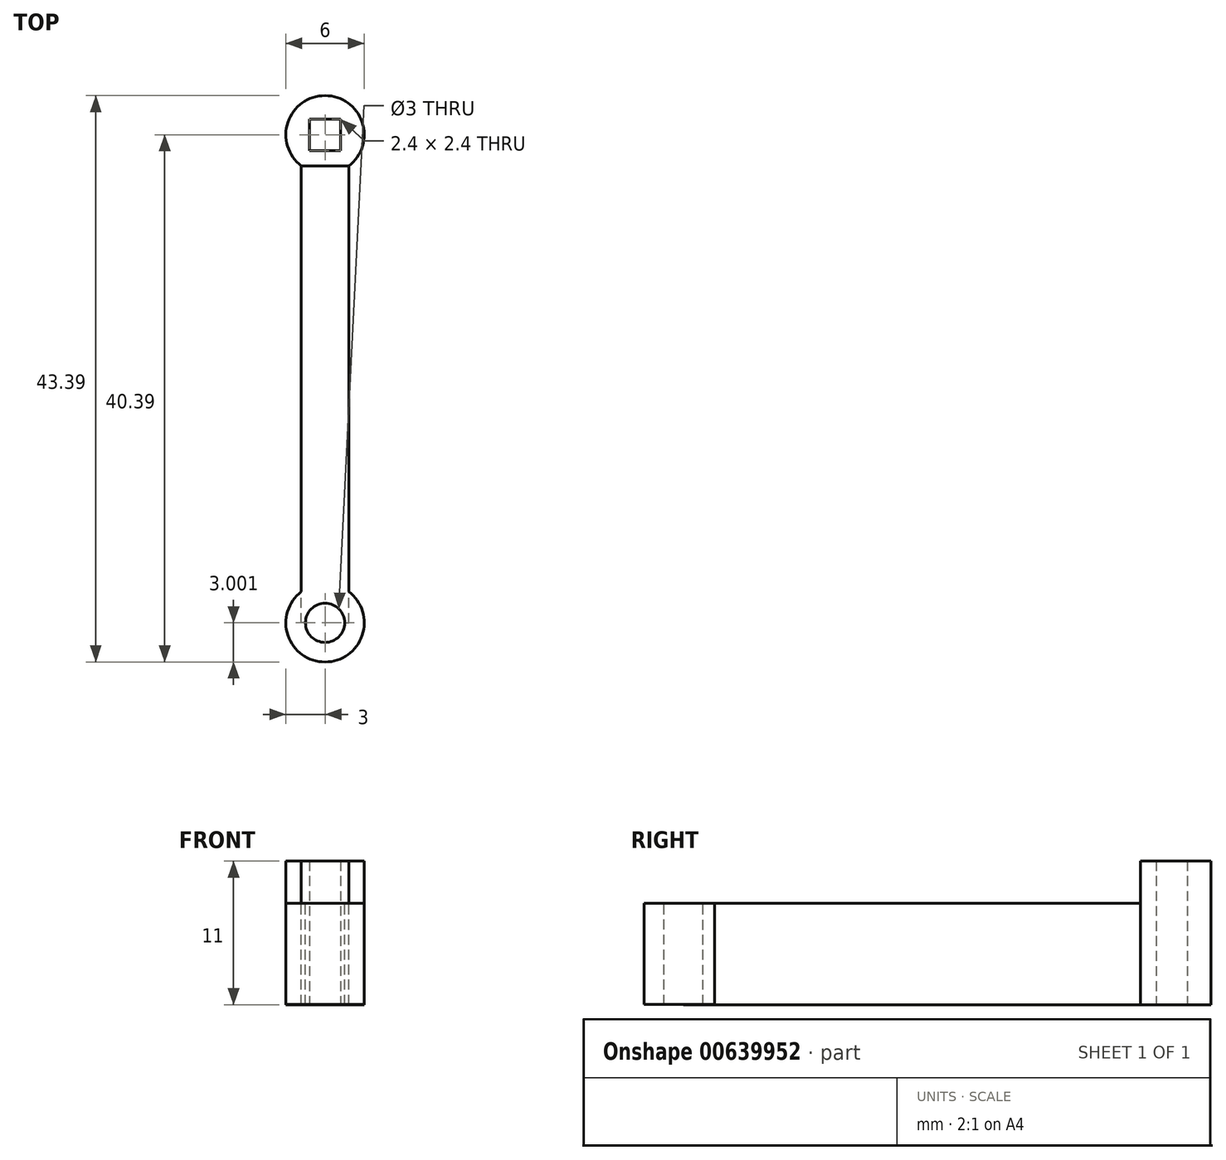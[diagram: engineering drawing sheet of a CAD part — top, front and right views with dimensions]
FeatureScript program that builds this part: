
annotation { "Feature Type Name" : "Feature", "Feature Type Description" : "" }
export const myFeature = defineFeature(function(context is Context, id is Id, definition is map)
    precondition{}
    {
        {
            var Q0;
            Q0=qCreatedBy(makeId("Top.planeOp"),FACE);
            var sketch = newSketch(context, id + "F0", { "sketchPlane" : qUnion([Q0])});
            skCircle(sketch, "E0", {"center": v(0, 0) * mm, "radius": 3 * mm});
            skLineSegment(sketch, "E1", {"start": v(0, 0) * mm, "end": v(0, -3) * mm});
            skLineSegment(sketch, "E2", {"start": v(0, 0) * mm, "end": v(0, 3) * mm});
            skPoint(sketch, "E3", {"position": v(0, -1.2) * mm});
            skPoint(sketch, "E4", {"position": v(0, 1.2) * mm});
            skLineSegment(sketch, "E5", {"start": v(0, 0) * mm, "end": v(3, 0) * mm});
            skLineSegment(sketch, "E6", {"start": v(0, 0) * mm, "end": v(-3, 0) * mm});
            skPoint(sketch, "E7", {"position": v(-1.2, 0) * mm});
            skPoint(sketch, "E8", {"position": v(1.2, 0) * mm});
            skPoint(sketch, "E9", {"position": v(-2.7, 2.32) * mm});
            skLineSegment(sketch, "E10", {"start": v(-1.2, 1.03) * mm, "end": v(-1.2, 0) * mm});
            skLineSegment(sketch, "E11", {"start": v(0, 1.2) * mm, "end": v(1.2, 1.2) * mm});
            skLineSegment(sketch, "E12", {"start": v(1.2, 1.2) * mm, "end": v(1.2, 0) * mm});
            skLineSegment(sketch, "E13", {"start": v(-1.2, 0) * mm, "end": v(-1.2, -1.2) * mm});
            skLineSegment(sketch, "E14", {"start": v(-1.2, -1.2) * mm, "end": v(0, -1.2) * mm});
            skLineSegment(sketch, "E15", {"start": v(0, -1.2) * mm, "end": v(1.2, -1.2) * mm});
            skLineSegment(sketch, "E16", {"start": v(1.2, -1.2) * mm, "end": v(1.2, 0) * mm});
            skLineSegment(sketch, "E17.top", {"start": v(-1.2, -1.2) * mm, "end": v(1.2, -1.2) * mm});
            skLineSegment(sketch, "E17.left", {"start": v(-1.2, 1.03) * mm, "end": v(-1.2, -1.2) * mm});
            skLineSegment(sketch, "E17.right", {"start": v(1.2, 0.86) * mm, "end": v(1.2, -1.2) * mm});
            skLineSegment(sketch, "E18.right", {"start": v(1.2, 1.03) * mm, "end": v(1.2, -1.2) * mm});
            skLineSegment(sketch, "E19.bottom", {"start": v(1.2, 1.2) * mm, "end": v(-1.2, 1.2) * mm});
            skLineSegment(sketch, "E19.top", {"start": v(1.2, -1.2) * mm, "end": v(-1.2, -1.2) * mm});
            skLineSegment(sketch, "E19.left", {"start": v(1.2, 1.2) * mm, "end": v(1.2, -1.2) * mm});
            skLineSegment(sketch, "E19.right", {"start": v(-1.2, 1.2) * mm, "end": v(-1.2, -1.2) * mm});
            skSolve(sketch);
        }
        {
            var Q0;
            Q0 = qSketchRegion(id + "F0", true);
            extrude(context, id + "F1", {"entities" : qUnion([Q0]), "depth" : 11 * mm, "offsetDistance" : 25 * mm});
        }
        {
            var Q0;
            Q0=makeQuery(id+"F1.opExtrude","CAP_FACE",FACE,{"disambiguationData":[OSD([sQuery(id+"F0.wireOp",EDGE,"E0"),sQuery(id+"F0.wireOp",EDGE,"E19.bottom"),sQuery(id+"F0.wireOp",EDGE,"E19.top"),sQuery(id+"F0.wireOp",EDGE,"E19.left"),sQuery(id+"F0.wireOp",EDGE,"E19.right")])],"isStart":false});
            var sketch = newSketch(context, id + "F2", { "sketchPlane" : qUnion([Q0])});
            skLineSegment(sketch, "E20", {"start": v(-1.81, -2.39) * mm, "end": v(1.81, -2.39) * mm});
            skSolve(sketch);
        }
        {
            var Q0;
            Q0 = qSketchRegion(id + "F2", true);
            var Q1;
            {var subQ0=sQuery(id+"F2.wireOp",EDGE,"E20");Q1=makeQuery(id+"F2.imprint","IMPRINT",FACE,{"disambiguationData":[TD([[makeQuery(id+"F2.imprint","IMPRINT",EDGE,{"derivedFrom":subQ0}),-1.0]])]});}
            extrude(context, id + "F3", {"entities" : qUnion([Q0, Q1]), "operationType" : NewBodyOperationType.REMOVE, "oppositeDirection" : true, "depth" : 25 * mm, "offsetDistance" : 25 * mm});
        }
        {
            var Q0;
            Q0=makeQuery(id+"F3.boolean.opBoolean","COPY",FACE,{"derivedFrom":makeQuery(id+"F3.opExtrude","SWEPT_FACE",FACE,{"disambiguationData":[OSD([sQuery(id+"F2.wireOp",EDGE,"E20")])]})});
            var sketch = newSketch(context, id + "F4", { "sketchPlane" : qUnion([Q0])});
            skLineSegment(sketch, "E21.bottom", {"start": v(-1.81, 0) * mm, "end": v(1.81, 0) * mm});
            skLineSegment(sketch, "E21.top", {"start": v(-1.81, 7.76) * mm, "end": v(1.81, 7.76) * mm});
            skLineSegment(sketch, "E21.left", {"start": v(-1.81, 0) * mm, "end": v(-1.81, 7.76) * mm});
            skLineSegment(sketch, "E21.right", {"start": v(1.81, 0) * mm, "end": v(1.81, 7.76) * mm});
            skSolve(sketch);
        }
        {
            var Q0;
            Q0=makeQuery(id+"F4.imprint","IMPRINT",FACE,{"disambiguationData":[TD([[makeQuery(id+"F4.imprint","IMPRINT",EDGE,{"derivedFrom":sQuery(id+"F4.wireOp",EDGE,"E21.bottom")}),1.0]])]});
            extrude(context, id + "F5", {"entities" : qUnion([Q0]), "operationType" : NewBodyOperationType.ADD, "depth" : 35 * mm, "offsetDistance" : 25 * mm});
        }
        {
            var Q0;
            Q0=makeQuery(id+"F5.opExtrude","SWEPT_FACE",FACE,{"disambiguationData":[OSD([sQuery(id+"F4.wireOp",EDGE,"E21.top")])]});
            var sketch = newSketch(context, id + "F6", { "sketchPlane" : qUnion([Q0])});
            skPoint(sketch, "E22", {"position": v(0, -37.39) * mm});
            skCircle(sketch, "E23", {"center": v(0, -37.39) * mm, "radius": 3 * mm});
            skSolve(sketch);
        }
        {
            var Q0;
            Q0 = qSketchRegion(id + "F6", true);
            extrude(context, id + "F7", {"entities" : qUnion([Q0]), "operationType" : NewBodyOperationType.ADD, "oppositeDirection" : true, "depth" : 7.75 * mm, "offsetDistance" : 25 * mm});
        }
        {
            var Q0;
            Q0=makeQuery(id+"F7.boolean.opBoolean","MERGE",FACE,{"derivedFrom":[makeQuery(id+"F5.opExtrude","SWEPT_FACE",FACE,{"disambiguationData":[OSD([sQuery(id+"F4.wireOp",EDGE,"E21.top")])]}),makeQuery(id+"F7.opExtrude","CAP_FACE",FACE,{"disambiguationData":[OSD([sQuery(id+"F6.wireOp",EDGE,"E23")])],"isStart":true})]});
            var sketch = newSketch(context, id + "F8", { "sketchPlane" : qUnion([Q0])});
            skPoint(sketch, "E24", {"position": v(0, -37.39) * mm});
            skCircle(sketch, "E25", {"center": v(0, -37.39) * mm, "radius": 1.5 * mm});
            skSolve(sketch);
        }
        {
            var Q0;
            Q0=makeQuery(id+"F8.imprint","IMPRINT",FACE,{"disambiguationData":[TD([[makeQuery(id+"F8.imprint","IMPRINT",EDGE,{"derivedFrom":sQuery(id+"F8.wireOp",EDGE,"E25")}),1.0]])]});
            extrude(context, id + "F9", {"entities" : qUnion([Q0]), "operationType" : NewBodyOperationType.REMOVE, "oppositeDirection" : true, "depth" : 25 * mm, "offsetDistance" : 25 * mm});
        }
    });
